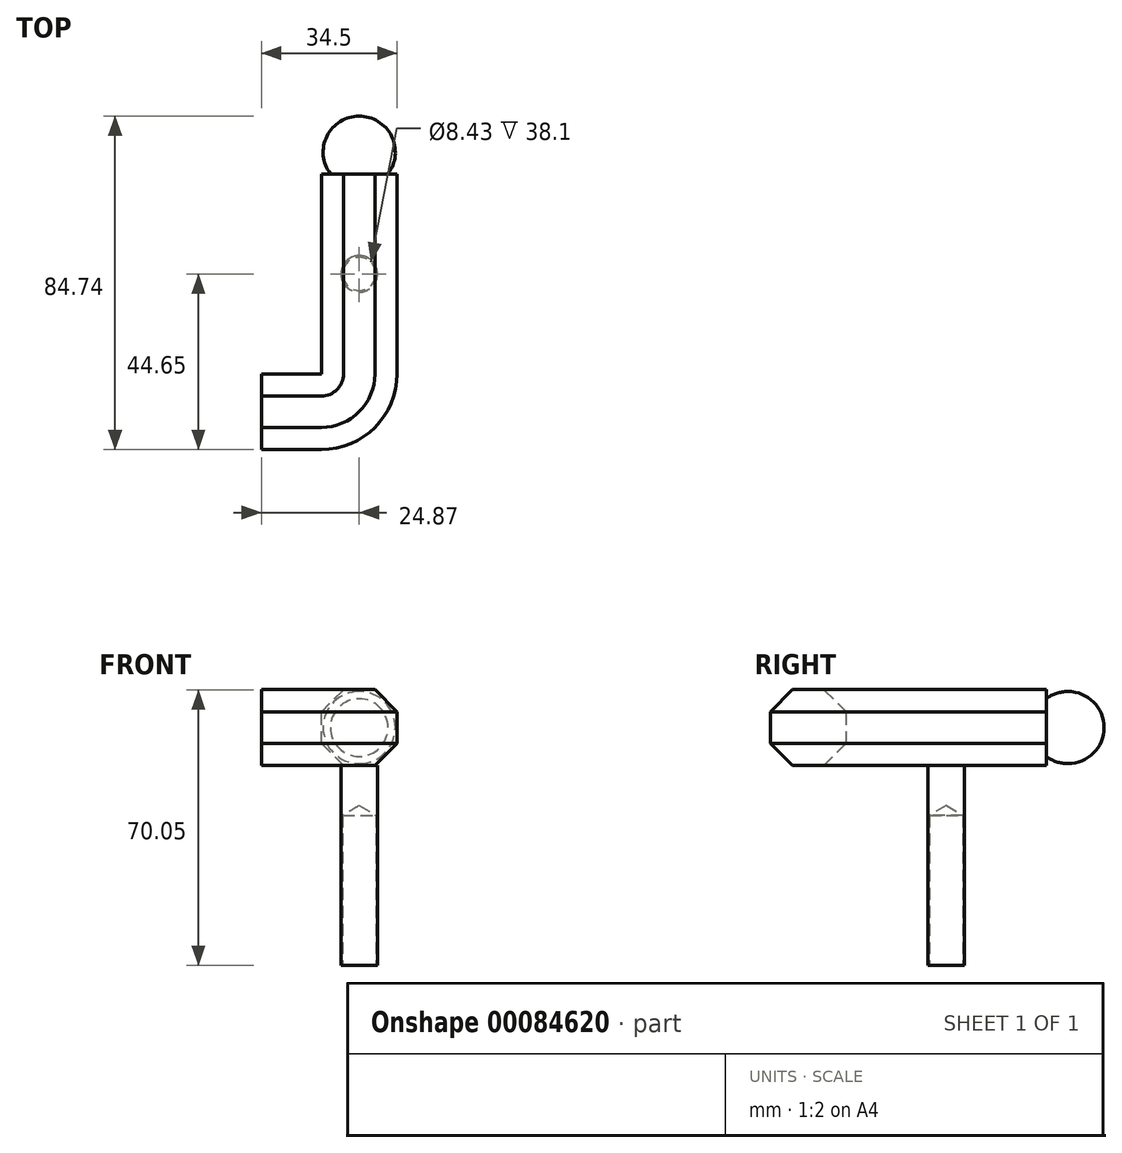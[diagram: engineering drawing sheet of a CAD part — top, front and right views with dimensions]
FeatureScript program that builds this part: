
annotation { "Feature Type Name" : "Feature", "Feature Type Description" : "" }
export const myFeature = defineFeature(function(context is Context, id is Id, definition is map)
    precondition{}
    {
        {
            var Q0;
            Q0=qCreatedBy(makeId("Top.planeOp"),FACE);
            var sketch = newSketch(context, id + "F0", { "sketchPlane" : qUnion([Q0])});
            skCircle(sketch, "E0", {"center": v(0, 0) * mm, "radius": 4.64 * mm});
            skSolve(sketch);
        }
        {
            var Q0;
            Q0=makeQuery(id+"F0.imprint","IMPRINT",FACE,{"disambiguationData":[TD([[makeQuery(id+"F0.imprint","IMPRINT",EDGE,{"derivedFrom":sQuery(id+"F0.wireOp",EDGE,"E0")}),1.0]])]});
            extrude(context, id + "F1", {"entities" : qUnion([Q0]), "depth" : 50.8 * mm});
        }
        {
            var Q0;
            Q0=sQuery(id+"F0.wireOp",VERTEX,"E0.center");
            var Q1;
            Q1=makeQuery(id+"F1.opExtrude","SWEPT_BODY",BODY,{"disambiguationData":[OSD([sQuery(id+"F0.wireOp",EDGE,"E0")])]});
            hole(context, id + "F2", {"style" : HoleStyle.SIMPLE, "endStyle" : HoleEndStyle.BLIND, "oppositeDirection" : true, "holeDiameter" : 8.43 * mm, "holeDepth" : 38.1 * mm, "locations" : qUnion([Q0]), "scope" : qUnion([Q1])});
        }
        {
            var Q0;
            Q0=qCreatedBy(makeId("Front.planeOp"),FACE);
            var sketch = newSketch(context, id + "F3", { "sketchPlane" : qUnion([Q0])});
            skCircle(sketch, "E1.cCircle", {"center": v(0, 60.43) * mm, "radius": 9.63 * mm, "construction": true});
            skLineSegment(sketch, "E1.0", {"start": v(-3.99, 50.8) * mm, "end": v(-9.63, 56.44) * mm});
            skLineSegment(sketch, "E1.1", {"start": v(-9.63, 56.44) * mm, "end": v(-9.63, 64.42) * mm});
            skLineSegment(sketch, "E1.2", {"start": v(-9.63, 64.42) * mm, "end": v(-3.99, 70.05) * mm});
            skLineSegment(sketch, "E1.3", {"start": v(-3.99, 70.05) * mm, "end": v(3.99, 70.05) * mm});
            skLineSegment(sketch, "E1.4", {"start": v(3.99, 70.05) * mm, "end": v(9.63, 64.42) * mm});
            skLineSegment(sketch, "E1.5", {"start": v(9.63, 64.42) * mm, "end": v(9.63, 56.44) * mm});
            skLineSegment(sketch, "E1.6", {"start": v(9.63, 56.44) * mm, "end": v(3.99, 50.8) * mm});
            skLineSegment(sketch, "E1.7", {"start": v(3.99, 50.8) * mm, "end": v(-3.99, 50.8) * mm});
            skPoint(sketch, "E1.0.midPoint", {"position": v(-6.8, 53.62) * mm});
            skLineSegment(sketch, "E2", {"start": v(0, 60.43) * mm, "end": v(0, 70.05) * mm});
            skSolve(sketch);
        }
        {
            var Q0;
            Q0=makeQuery(id+"F3.imprint","IMPRINT",FACE,{"disambiguationData":[TD([[makeQuery(id+"F3.imprint","IMPRINT",EDGE,{"derivedFrom":sQuery(id+"F3.wireOp",EDGE,"E1.0")}),-1.0]])]});
            extrude(context, id + "F4", {"entities" : qUnion([Q0]), "operationType" : NewBodyOperationType.ADD, "depth" : 25.4 * mm, "hasSecondDirection" : true, "secondDirectionOppositeDirection" : true, "secondDirectionDepth" : 25.4 * mm});
        }
        {
            var Q0;
            Q0=makeQuery(id+"F4.opExtrude","CAP_FACE",FACE,{"disambiguationData":[OSD([sQuery(id+"F3.wireOp",EDGE,"E1.0"),sQuery(id+"F3.wireOp",EDGE,"E1.1"),sQuery(id+"F3.wireOp",EDGE,"E1.2"),sQuery(id+"F3.wireOp",EDGE,"E1.3"),sQuery(id+"F3.wireOp",EDGE,"E1.4"),sQuery(id+"F3.wireOp",EDGE,"E1.5"),sQuery(id+"F3.wireOp",EDGE,"E1.6"),sQuery(id+"F3.wireOp",EDGE,"E1.7")])],"isStart":false});
            var Q1;
            Q1=makeQuery(id+"F4.opExtrude","CAP_EDGE",EDGE,{"disambiguationData":[OSD([sQuery(id+"F3.wireOp",EDGE,"E1.1")])],"isStart":false});
            revolve(context, id + "F5", {"operationType" : NewBodyOperationType.ADD, "entities" : qUnion([Q0]), "axis" : qUnion([Q1]), "revolveType" : RevolveType.ONE_DIRECTION, "oppositeDirection" : true, "angle" : 90 * degree});
        }
        {
            var Q0;
            Q0=makeQuery(id+"F4.opExtrude","CAP_FACE",FACE,{"disambiguationData":[OSD([sQuery(id+"F3.wireOp",EDGE,"E1.0"),sQuery(id+"F3.wireOp",EDGE,"E1.1"),sQuery(id+"F3.wireOp",EDGE,"E1.2"),sQuery(id+"F3.wireOp",EDGE,"E1.3"),sQuery(id+"F3.wireOp",EDGE,"E1.4"),sQuery(id+"F3.wireOp",EDGE,"E1.5"),sQuery(id+"F3.wireOp",EDGE,"E1.6"),sQuery(id+"F3.wireOp",EDGE,"E1.7")])],"isStart":true});
            var sketch = newSketch(context, id + "F6", { "sketchPlane" : qUnion([Q0])});
            skSolve(sketch);
        }
        {
            var Q0;
            Q0=qCreatedBy(makeId("Right.planeOp"),FACE);
            var sketch = newSketch(context, id + "F7", { "sketchPlane" : qUnion([Q0])});
            skCircle(sketch, "E3", {"center": v(30.92, 60.43) * mm, "radius": 9.17 * mm});
            skLineSegment(sketch, "E4", {"start": v(30.92, 60.43) * mm, "end": v(21.75, 60.43) * mm});
            skLineSegment(sketch, "E5", {"start": v(30.92, 69.6) * mm, "end": v(30.92, 51.26) * mm});
            skLineSegment(sketch, "E6", {"start": v(30.92, 60.43) * mm, "end": v(22.12, 63.01) * mm});
            skLineSegment(sketch, "E7", {"start": v(22.12, 63.01) * mm, "end": v(22.12, 57.84) * mm});
            skLineSegment(sketch, "E8", {"start": v(22.12, 57.84) * mm, "end": v(30.92, 60.43) * mm});
            skLineSegment(sketch, "E9", {"start": v(25.4, 62.05) * mm, "end": v(25.4, 58.8) * mm});
            skPoint(sketch, "E10", {"position": v(25.4, 53.1) * mm});
            skPoint(sketch, "E11", {"position": v(25.4, 67.75) * mm});
            skLineSegment(sketch, "E12", {"start": v(25.4, 67.75) * mm, "end": v(25.4, 62.05) * mm});
            skLineSegment(sketch, "E13", {"start": v(25.4, 58.8) * mm, "end": v(25.4, 53.1) * mm});
            skSolve(sketch);
        }
        {
            var Q0;
            {var subQ0=sQuery(id+"F7.wireOp",EDGE,"E5");var subQ1=sQuery(id+"F7.wireOp",EDGE,"E3");var subQ2=makeQuery(id+"F7.imprint","INTERSECT",VERTEX,{"disambiguationData":[OD(0.0)],"derivedFrom":[subQ1,subQ0]});Q0=makeQuery(id+"F7.imprint","IMPRINT",FACE,{"disambiguationData":[TD([[makeQuery(id+"F7.imprint","IMPRINT",EDGE,{"disambiguationData":[TD([[subQ2,1.0]])],"derivedFrom":subQ1}),1.0]])]});}
            var Q1;
            Q1=sQuery(id+"F7.wireOp",EDGE,"E5");
            revolve(context, id + "F8", {"operationType" : NewBodyOperationType.ADD, "entities" : qUnion([Q0]), "axis" : qUnion([Q1]), "revolveType" : RevolveType.FULL});
        }
        {
            var Q0;
            {var subQ0=sQuery(id+"F3.wireOp",EDGE,"E1.1");Q0=makeQuery(id+"F5.boolean.opBoolean","MERGE",FACE,{"derivedFrom":[makeQuery(id+"F4.opExtrude","SWEPT_FACE",FACE,{"disambiguationData":[OSD([subQ0])]}),makeQuery(id+"F5.opRevolve","CAP_FACE",FACE,{"disambiguationData":[OSD([sQuery(id+"F3.wireOp",EDGE,"E1.0"),subQ0,sQuery(id+"F3.wireOp",EDGE,"E1.2"),sQuery(id+"F3.wireOp",EDGE,"E1.3"),sQuery(id+"F3.wireOp",EDGE,"E1.4"),sQuery(id+"F3.wireOp",EDGE,"E1.5"),sQuery(id+"F3.wireOp",EDGE,"E1.6"),sQuery(id+"F3.wireOp",EDGE,"E1.7")])],"isStart":false})]});}
            var sketch = newSketch(context, id + "F9", { "sketchPlane" : qUnion([Q0])});
            skCircle(sketch, "E14.cCircle", {"center": v(35.03, 60.43) * mm, "radius": 9.63 * mm, "construction": true});
            skLineSegment(sketch, "E14.0", {"start": v(39.02, 50.8) * mm, "end": v(31.04, 50.8) * mm});
            skLineSegment(sketch, "E14.1", {"start": v(31.04, 50.8) * mm, "end": v(25.4, 56.44) * mm});
            skLineSegment(sketch, "E14.2", {"start": v(25.4, 56.44) * mm, "end": v(25.4, 64.42) * mm});
            skLineSegment(sketch, "E14.3", {"start": v(25.4, 64.42) * mm, "end": v(31.04, 70.05) * mm});
            skLineSegment(sketch, "E14.4", {"start": v(31.04, 70.05) * mm, "end": v(39.02, 70.05) * mm});
            skLineSegment(sketch, "E14.5", {"start": v(39.02, 70.05) * mm, "end": v(44.65, 64.42) * mm});
            skLineSegment(sketch, "E14.6", {"start": v(44.65, 64.42) * mm, "end": v(44.65, 56.44) * mm});
            skLineSegment(sketch, "E14.7", {"start": v(44.65, 56.44) * mm, "end": v(39.02, 50.8) * mm});
            skPoint(sketch, "E14.0.midPoint", {"position": v(35.03, 50.8) * mm});
            skSolve(sketch);
        }
        {
            var Q0;
            Q0 = qSketchRegion(id + "F9", true);
            extrude(context, id + "F10", {"entities" : qUnion([Q0]), "operationType" : NewBodyOperationType.ADD, "depth" : 15.24 * mm});
        }
    });
